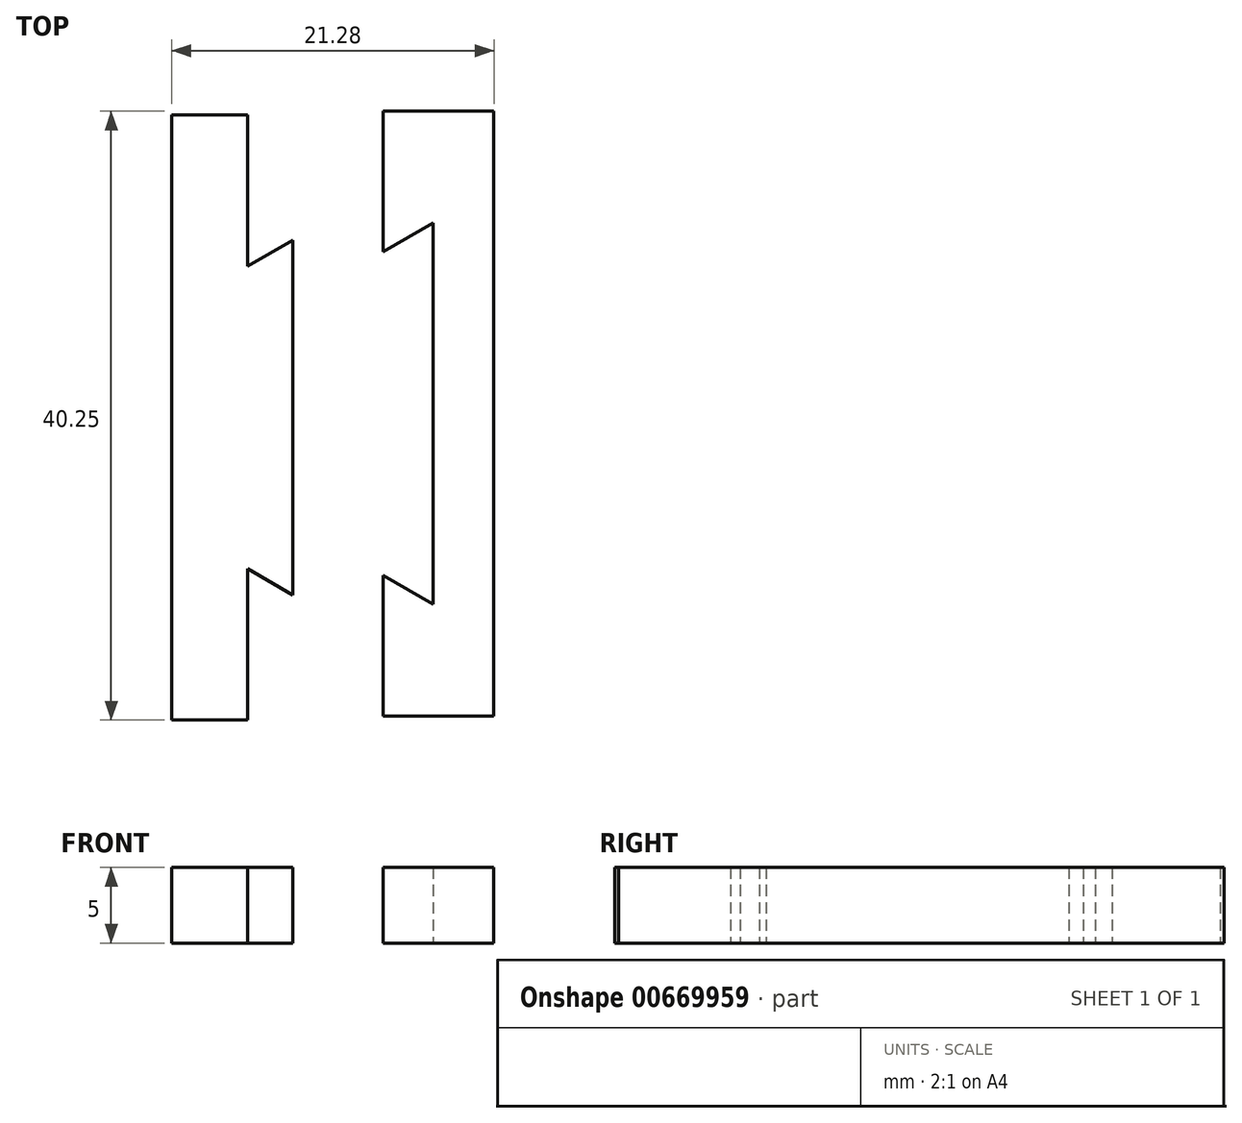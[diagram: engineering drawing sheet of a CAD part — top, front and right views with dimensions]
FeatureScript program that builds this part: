
annotation { "Feature Type Name" : "Feature", "Feature Type Description" : "" }
export const myFeature = defineFeature(function(context is Context, id is Id, definition is map)
    precondition{}
    {
        {
            var Q0;
            Q0=qCreatedBy(makeId("Top.planeOp"),FACE);
            var sketch = newSketch(context, id + "F0", { "sketchPlane" : qUnion([Q0])});
            skLineSegment(sketch, "E0", {"start": v(-12.35, 21.58) * mm, "end": v(-12.35, -18.42) * mm});
            skLineSegment(sketch, "E1", {"start": v(-12.35, 11.58) * mm, "end": v(-9.35, 13.3) * mm});
            skLineSegment(sketch, "E2", {"start": v(-9.35, 13.3) * mm, "end": v(-9.35, -10.15) * mm});
            skLineSegment(sketch, "E3", {"start": v(-9.35, -10.15) * mm, "end": v(-12.35, -8.42) * mm});
            skLineSegment(sketch, "E4", {"start": v(-12.35, 21.58) * mm, "end": v(-17.35, 21.58) * mm});
            skLineSegment(sketch, "E5", {"start": v(-17.35, 21.58) * mm, "end": v(-17.35, -18.42) * mm});
            skLineSegment(sketch, "E6", {"start": v(-17.35, -18.42) * mm, "end": v(-12.35, -18.42) * mm});
            skSolve(sketch);
        }
        {
            var Q0;
            Q0=qCreatedBy(makeId("Top.planeOp"),FACE);
            var sketch = newSketch(context, id + "F1", { "sketchPlane" : qUnion([Q0])});
            skLineSegment(sketch, "E7", {"start": v(-3.37, 21.83) * mm, "end": v(-3.37, 12.53) * mm});
            skLineSegment(sketch, "E8", {"start": v(-3.37, 12.53) * mm, "end": v(-0.07, 14.43) * mm});
            skLineSegment(sketch, "E9", {"start": v(-0.07, 14.43) * mm, "end": v(-0.07, -10.78) * mm});
            skLineSegment(sketch, "E10", {"start": v(-0.07, -10.78) * mm, "end": v(-3.37, -8.87) * mm});
            skLineSegment(sketch, "E11", {"start": v(-3.37, -8.87) * mm, "end": v(-3.37, -18.17) * mm});
            skLineSegment(sketch, "E12", {"start": v(-3.37, -18.17) * mm, "end": v(3.93, -18.17) * mm});
            skLineSegment(sketch, "E13", {"start": v(3.93, -18.17) * mm, "end": v(3.93, 21.83) * mm});
            skLineSegment(sketch, "E14", {"start": v(3.93, 21.83) * mm, "end": v(-3.37, 21.83) * mm});
            skSolve(sketch);
        }
        {
            var Q0;
            {var subQ3=sQuery(id+"F0.wireOp",EDGE,"E4");Q0=makeQuery(id+"F0.imprint","IMPRINT",FACE,{"disambiguationData":[TD([[makeQuery(id+"F0.imprint","IMPRINT",EDGE,{"derivedFrom":subQ3}),1.0]])]});}
            var Q1;
            {var subQ0=sQuery(id+"F0.wireOp",EDGE,"E1");Q1=makeQuery(id+"F0.imprint","IMPRINT",FACE,{"disambiguationData":[TD([[makeQuery(id+"F0.imprint","IMPRINT",EDGE,{"derivedFrom":subQ0}),-1.0]])]});}
            var Q2;
            Q2=makeQuery(id+"F1.imprint","IMPRINT",FACE,{"disambiguationData":[TD([[makeQuery(id+"F1.imprint","IMPRINT",EDGE,{"derivedFrom":sQuery(id+"F1.wireOp",EDGE,"E7")}),1.0]])]});
            extrude(context, id + "F2", {"entities" : qUnion([Q0, Q1, Q2]), "depth" : 5 * mm, "offsetDistance" : 25 * mm});
        }
    });
